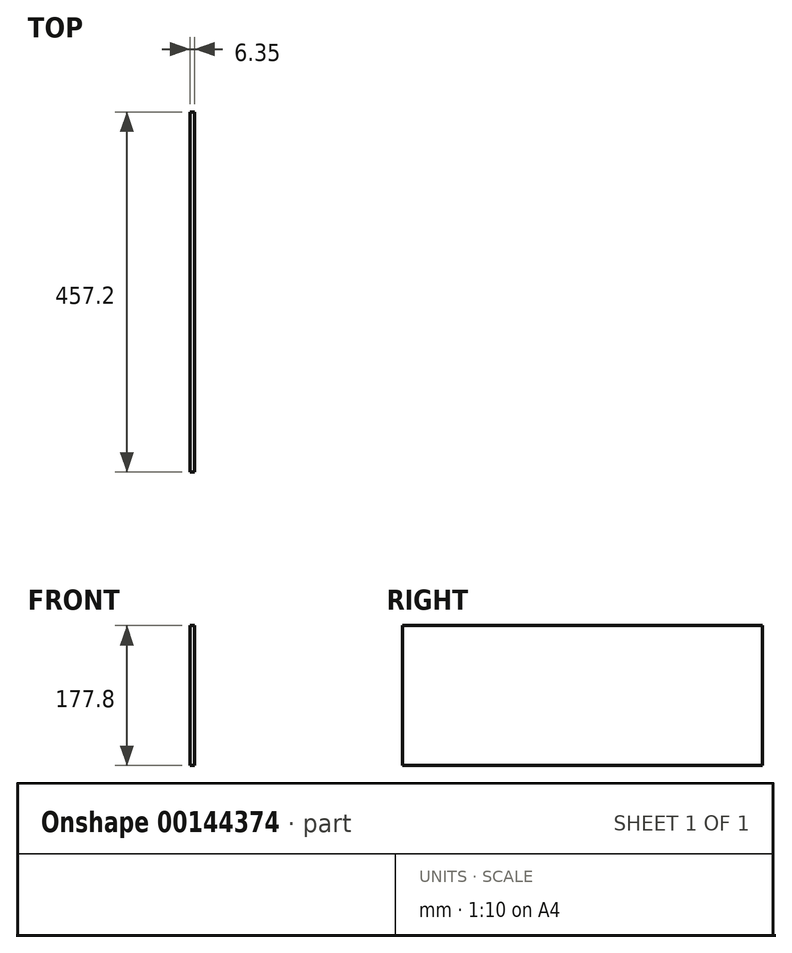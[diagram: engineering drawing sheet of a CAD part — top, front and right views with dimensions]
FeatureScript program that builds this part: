
annotation { "Feature Type Name" : "Feature", "Feature Type Description" : "" }
export const myFeature = defineFeature(function(context is Context, id is Id, definition is map)
    precondition{}
    {
        {
            var Q0;
            Q0=qCreatedBy(makeId("Right.planeOp"),FACE);
            var sketch = newSketch(context, id + "F0", { "sketchPlane" : qUnion([Q0])});
            skLineSegment(sketch, "E0", {"start": v(0, 0) * mm, "end": v(0, 177.8) * mm});
            skLineSegment(sketch, "E1", {"start": v(0, 177.8) * mm, "end": v(-457.2, 177.8) * mm});
            skLineSegment(sketch, "E2", {"start": v(-457.2, 177.8) * mm, "end": v(-457.2, 0) * mm});
            skLineSegment(sketch, "E3", {"start": v(-457.2, 0) * mm, "end": v(0, 0) * mm});
            skSolve(sketch);
        }
        {
            var Q0;
            Q0=qSketchRegion(id+"F0",true);
            extrude(context, id + "F1", {"entities" : qUnion([Q0]), "depth" : 6.35 * mm});
        }
    });
